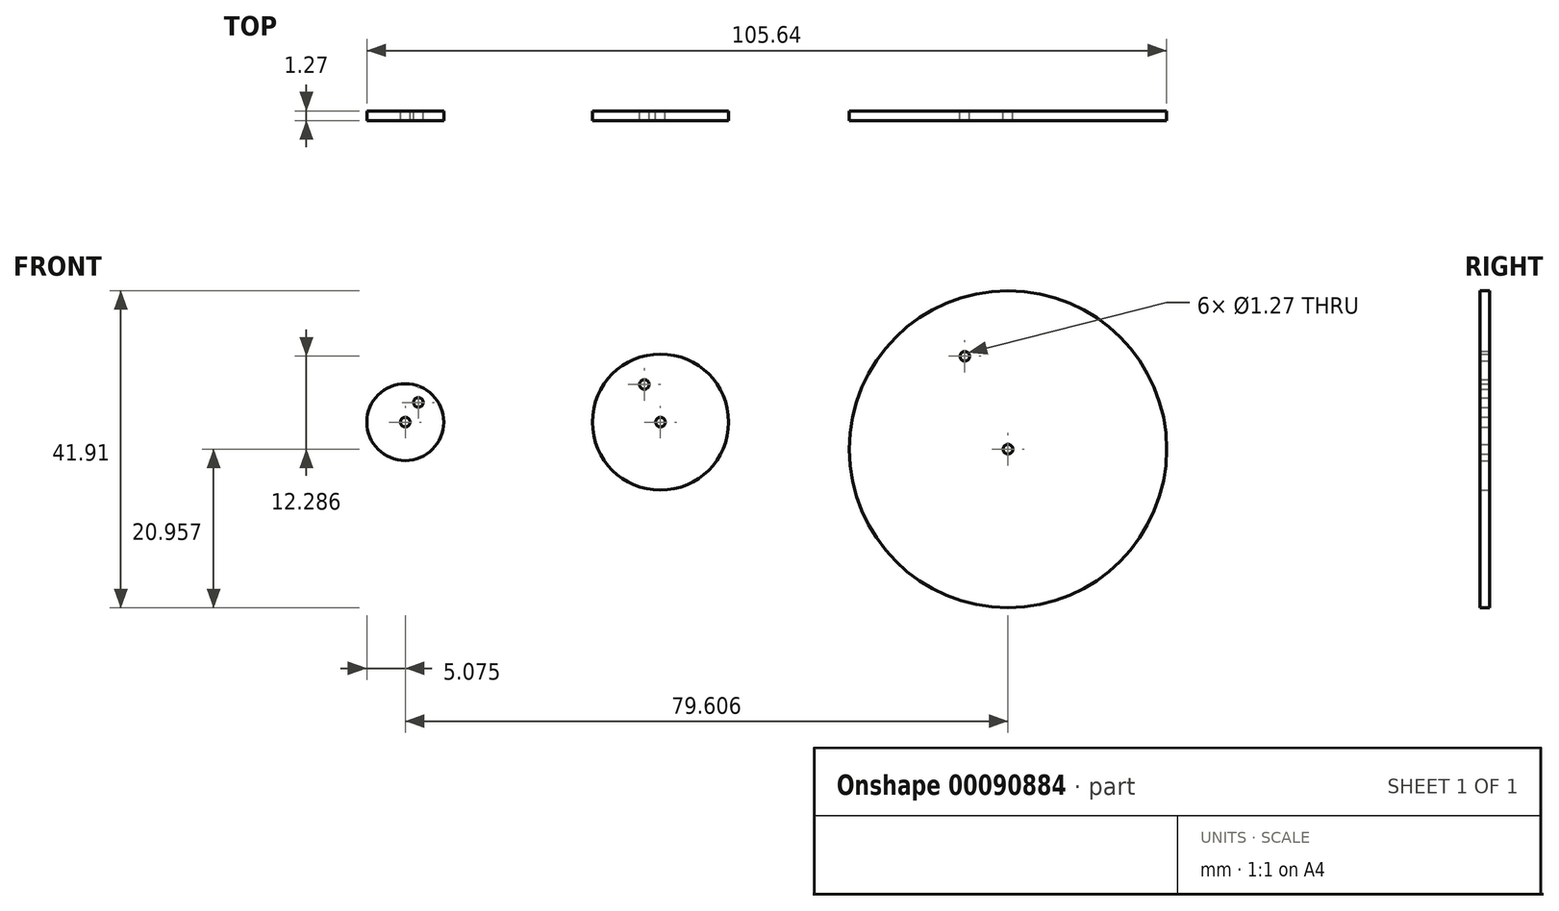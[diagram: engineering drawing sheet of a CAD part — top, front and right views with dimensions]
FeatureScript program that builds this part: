
annotation { "Feature Type Name" : "Feature", "Feature Type Description" : "" }
export const myFeature = defineFeature(function(context is Context, id is Id, definition is map)
    precondition{}
    {
        {
            var Q0;
            Q0=qCreatedBy(makeId("Front.planeOp"),FACE);
            var sketch = newSketch(context, id + "F0", { "sketchPlane" : qUnion([Q0])});
            skCircle(sketch, "E0", {"center": v(-55.4, 0) * mm, "radius": 5.08 * mm});
            skCircle(sketch, "E1", {"center": v(-21.7, 0) * mm, "radius": 9 * mm});
            skCircle(sketch, "E2", {"center": v(24.21, -3.58) * mm, "radius": 20.96 * mm});
            skCircle(sketch, "E3", {"center": v(-55.4, 0) * mm, "radius": 0.64 * mm});
            skCircle(sketch, "E4", {"center": v(-21.7, 0) * mm, "radius": 0.64 * mm});
            skCircle(sketch, "E5", {"center": v(24.21, -3.58) * mm, "radius": 0.64 * mm});
            skCircle(sketch, "E6", {"center": v(-53.67, 2.6) * mm, "radius": 0.64 * mm});
            skCircle(sketch, "E7", {"center": v(-23.82, 4.98) * mm, "radius": 0.64 * mm});
            skCircle(sketch, "E8", {"center": v(18.5, 8.7) * mm, "radius": 0.64 * mm});
            skSolve(sketch);
        }
        {
            var Q0;
            Q0=makeQuery(id+"F0.imprint","IMPRINT",FACE,{"disambiguationData":[TD([[makeQuery(id+"F0.imprint","IMPRINT",EDGE,{"derivedFrom":sQuery(id+"F0.wireOp",EDGE,"E0")}),1.0]])]});
            extrude(context, id + "F1", {"entities" : qUnion([Q0]), "depth" : 1.27 * mm});
        }
        {
            var Q0;
            Q0 = qSketchRegion(id + "F0", true);
            extrude(context, id + "F2", {"entities" : qUnion([Q0]), "operationType" : NewBodyOperationType.ADD, "depth" : 1.27 * mm});
        }
    });
